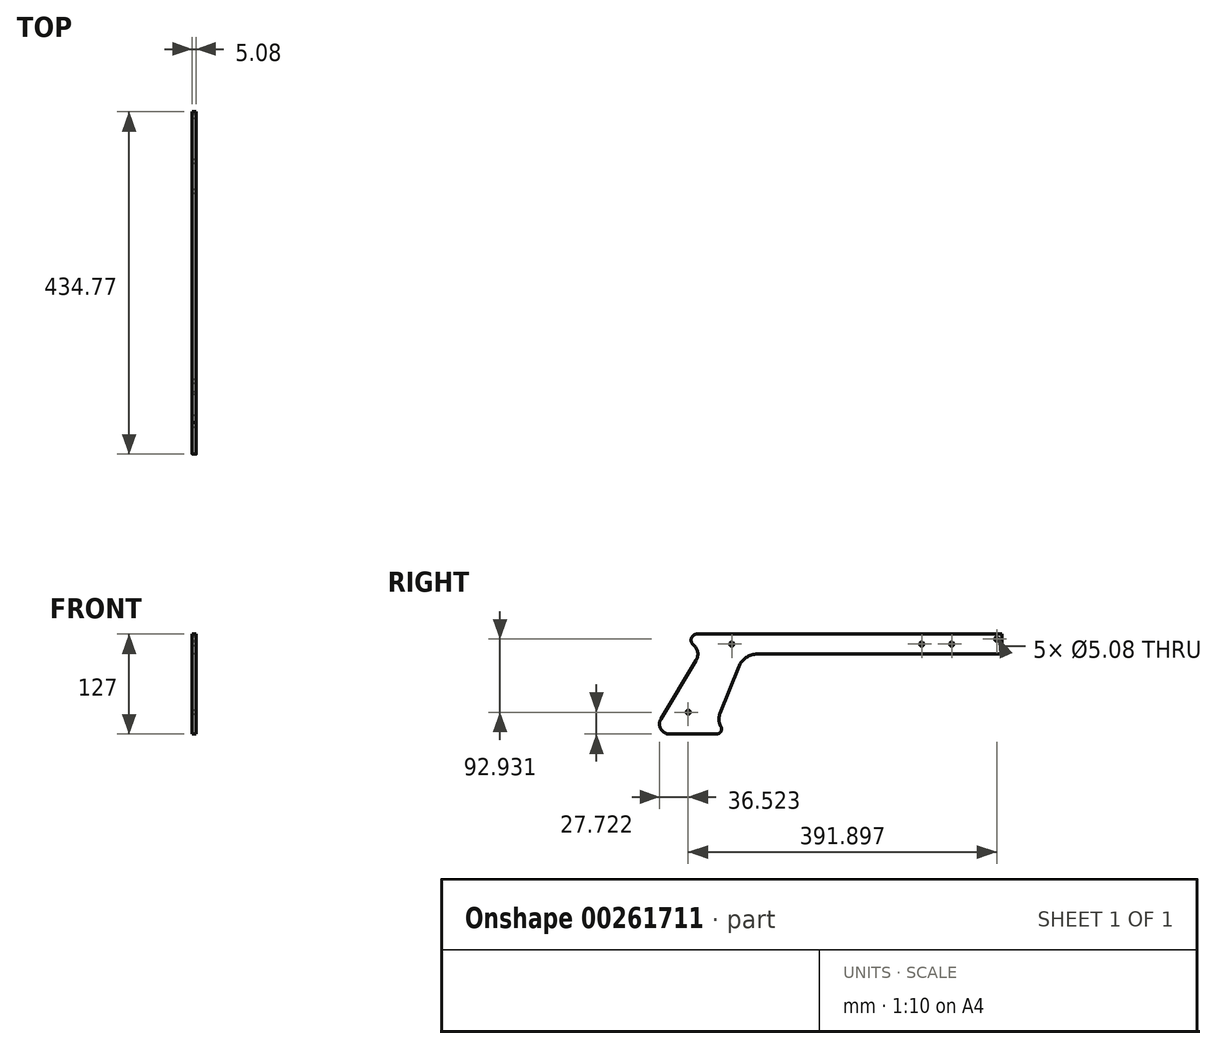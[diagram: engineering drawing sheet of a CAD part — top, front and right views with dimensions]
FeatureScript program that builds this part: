
annotation { "Feature Type Name" : "Feature", "Feature Type Description" : "" }
export const myFeature = defineFeature(function(context is Context, id is Id, definition is map)
    precondition{}
    {
        {
            var Q0;
            Q0=qCreatedBy(makeId("Right.planeOp"),FACE);
            var sketch = newSketch(context, id + "F0", { "sketchPlane" : qUnion([Q0])});
            skLineSegment(sketch, "E0.bottom", {"start": v(-604.49, -223.4) * mm, "end": v(-286.99, -223.4) * mm});
            skLineSegment(sketch, "E0.top", {"start": v(-604.49, -248.8) * mm, "end": v(-286.99, -248.8) * mm});
            skLineSegment(sketch, "E0.left", {"start": v(-604.49, -223.4) * mm, "end": v(-604.49, -248.8) * mm});
            skLineSegment(sketch, "E0.right", {"start": v(-286.99, -223.4) * mm, "end": v(-286.99, -248.8) * mm});
            skLineSegment(sketch, "E1", {"start": v(-604.49, -223.4) * mm, "end": v(-680.69, -350.4) * mm});
            skLineSegment(sketch, "E2", {"start": v(-680.69, -350.4) * mm, "end": v(-604.49, -350.4) * mm});
            skLineSegment(sketch, "E3", {"start": v(-604.49, -350.4) * mm, "end": v(-553.69, -223.4) * mm});
            skLineSegment(sketch, "E4", {"start": v(-325.09, -223.4) * mm, "end": v(-325.09, -248.8) * mm});
            skCircle(sketch, "E5", {"center": v(-579.09, -236.1) * mm, "radius": 2.54 * mm});
            skCircle(sketch, "E6", {"center": v(-634.44, -322.69) * mm, "radius": 2.54 * mm});
            skLineSegment(sketch, "E7.bottom", {"start": v(-286.99, -223.4) * mm, "end": v(-236.19, -223.4) * mm});
            skLineSegment(sketch, "E7.top", {"start": v(-286.99, -248.8) * mm, "end": v(-236.19, -248.8) * mm});
            skLineSegment(sketch, "E7.right", {"start": v(-236.19, -223.4) * mm, "end": v(-236.19, -248.8) * mm});
            skCircle(sketch, "E8", {"center": v(-242.54, -229.76) * mm, "radius": 2.54 * mm});
            skCircle(sketch, "E9", {"center": v(-299.69, -236.1) * mm, "radius": 2.54 * mm});
            skCircle(sketch, "E10", {"center": v(-337.79, -236.1) * mm, "radius": 2.54 * mm});
            skLineSegment(sketch, "E11", {"start": v(-604.49, -223.4) * mm, "end": v(-654.8, -223.4) * mm});
            skLineSegment(sketch, "E12", {"start": v(-604.49, -350.4) * mm, "end": v(-568.9, -350.4) * mm});
            skCircle(sketch, "E13", {"center": v(-637.5, -248.8) * mm, "radius": 15.24 * mm});
            skCircle(sketch, "E14", {"center": v(-623.13, -231.03) * mm, "radius": 7.62 * mm});
            skCircle(sketch, "E15", {"center": v(-658.26, -337.7) * mm, "radius": 12.7 * mm});
            skCircle(sketch, "E16", {"center": v(-576.35, -331.36) * mm, "radius": 19.05 * mm});
            skCircle(sketch, "E17", {"center": v(-598.35, -344.06) * mm, "radius": 6.35 * mm});
            skCircle(sketch, "E18", {"center": v(-546.65, -274.2) * mm, "radius": 25.4 * mm});
            skSolve(sketch);
        }
        {
            var Q0;
            {var subQ0=sQuery(id+"F0.wireOp",EDGE,"E14");var subQ1=makeQuery(id+"F0.imprint","INTERSECT",VERTEX,{"derivedFrom":[sQuery(id+"F0.wireOp",EDGE,"E11"),subQ0]});Q0=makeQuery(id+"F0.imprint","IMPRINT",FACE,{"disambiguationData":[TD([[makeQuery(id+"F0.imprint","IMPRINT",EDGE,{"disambiguationData":[TD([[subQ1,-1.0]])],"derivedFrom":subQ0}),1.0]])]});}
            var Q1;
            {var subQ0=sQuery(id+"F0.wireOp",EDGE,"E12");var subQ3=sQuery(id+"F0.wireOp",EDGE,"E17");var subQ5=makeQuery(id+"F0.imprint","INTERSECT",VERTEX,{"derivedFrom":[subQ0,subQ3]});Q1=makeQuery(id+"F0.imprint","IMPRINT",FACE,{"disambiguationData":[TD([[makeQuery(id+"F0.imprint","IMPRINT",EDGE,{"disambiguationData":[TD([[subQ5,1.0]])],"derivedFrom":subQ3}),-1.0]])]});}
            var Q2;
            Q2=makeQuery(id+"F0.imprint","IMPRINT",FACE,{"disambiguationData":[TD([[makeQuery(id+"F0.imprint","IMPRINT",EDGE,{"derivedFrom":sQuery(id+"F0.wireOp",EDGE,"E7.bottom")}),-1.0]])]});
            var Q3;
            {var subQ0=sQuery(id+"F0.wireOp",EDGE,"E15");var subQ1=makeQuery(id+"F0.imprint","INTERSECT",VERTEX,{"derivedFrom":[sQuery(id+"F0.wireOp",EDGE,"E1"),subQ0]});Q3=makeQuery(id+"F0.imprint","IMPRINT",FACE,{"disambiguationData":[TD([[makeQuery(id+"F0.imprint","IMPRINT",EDGE,{"disambiguationData":[TD([[subQ1,-1.0]])],"derivedFrom":subQ0}),1.0]])]});}
            var Q4;
            {var subQ0=sQuery(id+"F0.wireOp",EDGE,"E0.left");Q4=makeQuery(id+"F0.imprint","IMPRINT",FACE,{"disambiguationData":[TD([[makeQuery(id+"F0.imprint","IMPRINT",EDGE,{"derivedFrom":subQ0}),1.0]])]});}
            var Q5;
            {var subQ2=sQuery(id+"F0.wireOp",EDGE,"E4");Q5=makeQuery(id+"F0.imprint","IMPRINT",FACE,{"disambiguationData":[TD([[makeQuery(id+"F0.imprint","IMPRINT",EDGE,{"derivedFrom":subQ2}),1.0]])]});}
            var Q6;
            {var subQ0=sQuery(id+"F0.wireOp",EDGE,"E18");var subQ1=sQuery(id+"F0.wireOp",EDGE,"E0.top");var subQ2=makeQuery(id+"F0.imprint","INTERSECT",VERTEX,{"derivedFrom":[subQ1,subQ0]});Q6=makeQuery(id+"F0.imprint","IMPRINT",FACE,{"disambiguationData":[TD([[makeQuery(id+"F0.imprint","IMPRINT",EDGE,{"disambiguationData":[TD([[subQ2,1.0]])],"derivedFrom":subQ1}),-1.0]])]});}
            var Q7;
            {var subQ1=sQuery(id+"F0.wireOp",EDGE,"E1");var subQ3=sQuery(id+"F0.wireOp",EDGE,"E13");var subQ4=makeQuery(id+"F0.imprint","INTERSECT",VERTEX,{"derivedFrom":[subQ1,subQ3]});Q7=makeQuery(id+"F0.imprint","IMPRINT",FACE,{"disambiguationData":[TD([[makeQuery(id+"F0.imprint","IMPRINT",EDGE,{"disambiguationData":[TD([[subQ4,-1.0]])],"derivedFrom":subQ3}),-1.0]])]});}
            var Q8;
            {var subQ0=sQuery(id+"F0.wireOp",EDGE,"E16");var subQ1=sQuery(id+"F0.wireOp",EDGE,"E3");var subQ2=makeQuery(id+"F0.imprint","INTERSECT",VERTEX,{"derivedFrom":[subQ1,subQ0]});Q8=makeQuery(id+"F0.imprint","IMPRINT",FACE,{"disambiguationData":[TD([[makeQuery(id+"F0.imprint","IMPRINT",EDGE,{"disambiguationData":[TD([[subQ2,1.0]])],"derivedFrom":subQ1}),-1.0]])]});}
            var Q9;
            {var subQ5=sQuery(id+"F0.wireOp",EDGE,"E4");Q9=makeQuery(id+"F0.imprint","IMPRINT",FACE,{"disambiguationData":[TD([[makeQuery(id+"F0.imprint","IMPRINT",EDGE,{"derivedFrom":subQ5}),-1.0]])]});}
            var Q10;
            {var subQ0=sQuery(id+"F0.wireOp",EDGE,"E17");var subQ1=sQuery(id+"F0.wireOp",EDGE,"E3");var subQ2=makeQuery(id+"F0.imprint","INTERSECT",VERTEX,{"disambiguationData":[OD(0.0)],"derivedFrom":[subQ1,subQ0]});Q10=makeQuery(id+"F0.imprint","IMPRINT",FACE,{"disambiguationData":[TD([[makeQuery(id+"F0.imprint","IMPRINT",EDGE,{"disambiguationData":[TD([[subQ2,-1.0]])],"derivedFrom":subQ1}),-1.0]])]});}
            var Q11;
            {var subQ12=sQuery(id+"F0.wireOp",EDGE,"E0.left");Q11=makeQuery(id+"F0.imprint","IMPRINT",FACE,{"disambiguationData":[TD([[makeQuery(id+"F0.imprint","IMPRINT",EDGE,{"derivedFrom":subQ12}),-1.0]])]});}
            var Q12;
            {var subQ0=sQuery(id+"F0.wireOp",EDGE,"E17");var subQ1=sQuery(id+"F0.wireOp",EDGE,"E3");var subQ2=makeQuery(id+"F0.imprint","INTERSECT",VERTEX,{"disambiguationData":[OD(0.0)],"derivedFrom":[subQ1,subQ0]});Q12=makeQuery(id+"F0.imprint","IMPRINT",FACE,{"disambiguationData":[TD([[makeQuery(id+"F0.imprint","IMPRINT",EDGE,{"disambiguationData":[TD([[subQ2,-1.0]])],"derivedFrom":subQ1}),1.0]])]});}
            var Q13;
            {var subQ0=sQuery(id+"F0.wireOp",EDGE,"E7.right");Q13=makeQuery(id+"F0.imprint","IMPRINT",FACE,{"disambiguationData":[TD([[makeQuery(id+"F0.imprint","IMPRINT",EDGE,{"derivedFrom":subQ0}),-1.0]])]});}
            extrude(context, id + "F1", {"entities" : qUnion([Q0, Q1, Q2, Q3, Q4, Q5, Q6, Q7, Q8, Q9, Q10, Q11, Q12, Q13]), "offsetDistance" : 25.4 * mm, "depth" : 5.08 * mm});
        }
    });
